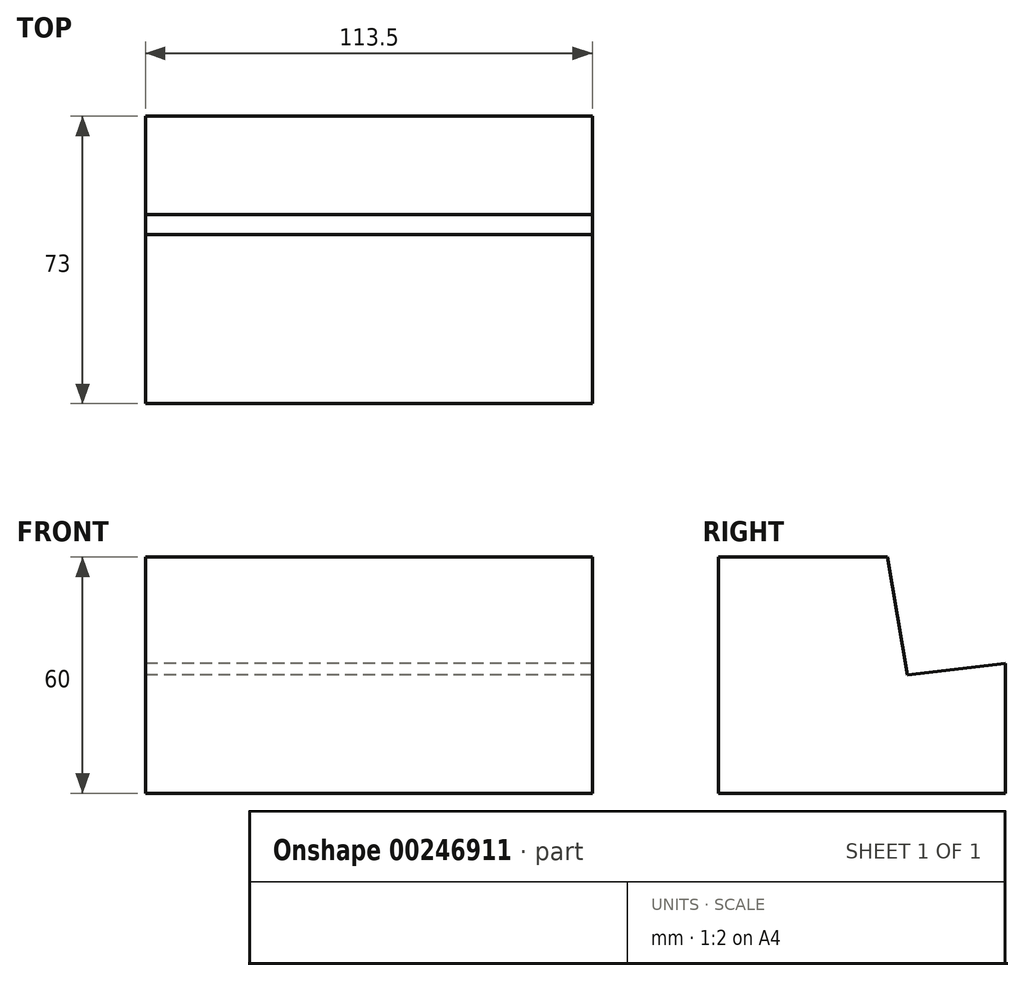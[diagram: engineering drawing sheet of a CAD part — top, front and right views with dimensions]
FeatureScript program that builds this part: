
annotation { "Feature Type Name" : "Feature", "Feature Type Description" : "" }
export const myFeature = defineFeature(function(context is Context, id is Id, definition is map)
    precondition{}
    {
        {
            var Q0;
            Q0=qCreatedBy(makeId("Right.planeOp"),FACE);
            var sketch = newSketch(context, id + "F0", { "sketchPlane" : qUnion([Q0])});
            skLineSegment(sketch, "E0.top", {"start": v(36.5, -30) * mm, "end": v(-36.5, -30) * mm});
            skLineSegment(sketch, "E0.right", {"start": v(-36.5, 30) * mm, "end": v(-36.5, -30) * mm});
            skPoint(sketch, "E0.middle", {"position": v(0, 0) * mm});
            skPoint(sketch, "E1", {"position": v(36.5, 3) * mm});
            skPoint(sketch, "E2", {"position": v(6.5, 30) * mm});
            skPoint(sketch, "E3", {"position": v(11.5, 0) * mm});
            skLineSegment(sketch, "E4", {"start": v(6.5, 30) * mm, "end": v(11.5, 0) * mm});
            skLineSegment(sketch, "E5", {"start": v(36.5, 3) * mm, "end": v(11.5, 0) * mm});
            skLineSegment(sketch, "E6", {"start": v(-36.5, 30) * mm, "end": v(6.5, 30) * mm});
            skLineSegment(sketch, "E7", {"start": v(36.5, 3) * mm, "end": v(36.5, -30) * mm});
            skSolve(sketch);
        }
        {
            var Q0;
            Q0=makeQuery(id+"F0.imprint","IMPRINT",FACE,{"disambiguationData":[TD([[makeQuery(id+"F0.imprint","IMPRINT",EDGE,{"derivedFrom":sQuery(id+"F0.wireOp",EDGE,"E0.top")}),-1.0]])]});
            extrude(context, id + "F1", {"entities" : qUnion([Q0]), "depth" : 113.5 * mm});
        }
    });
